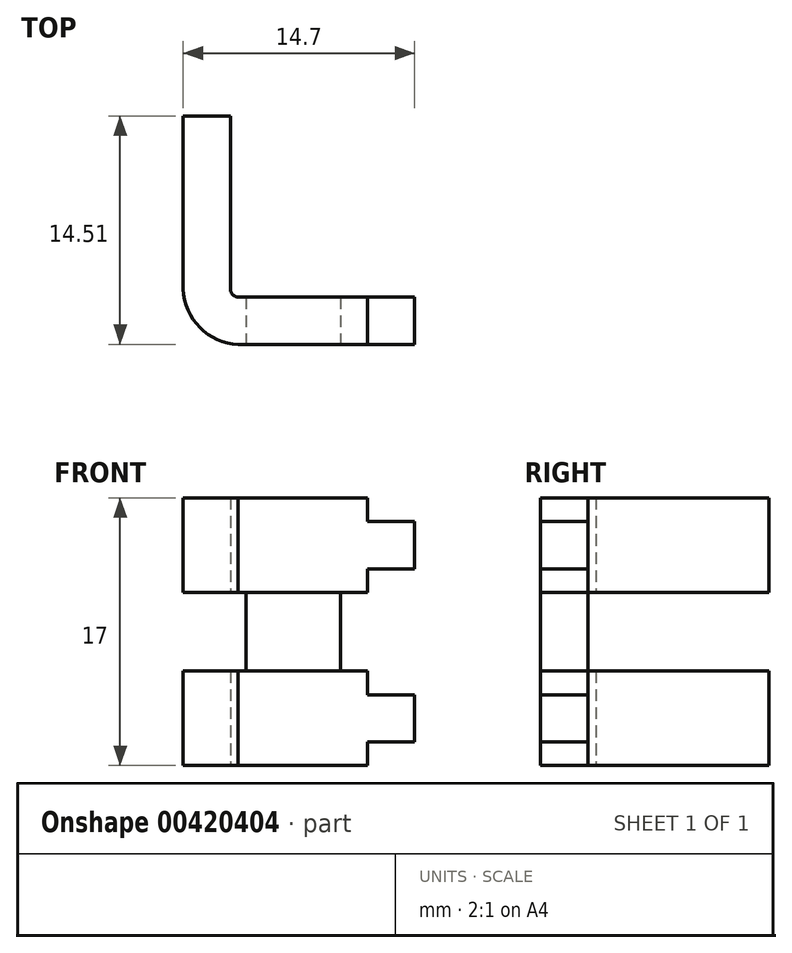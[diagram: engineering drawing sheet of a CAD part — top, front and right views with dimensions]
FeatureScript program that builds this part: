
annotation { "Feature Type Name" : "Feature", "Feature Type Description" : "" }
export const myFeature = defineFeature(function(context is Context, id is Id, definition is map)
    precondition{}
    {
        {
            var Q0;
            Q0=qCreatedBy(makeId("Top.planeOp"),FACE);
            var sketch = newSketch(context, id + "F0", { "sketchPlane" : qUnion([Q0])});
            skLineSegment(sketch, "E0", {"start": v(-1.5, 13) * mm, "end": v(1.5, 13) * mm});
            skLineSegment(sketch, "E1", {"start": v(13.2, 1.49) * mm, "end": v(13.2, -1.51) * mm});
            skArc(sketch, "E2", {"start": v(1.5, 2) * mm, "mid": v(1.65, 1.65) * mm, "end": v(2, 1.5) * mm});
            skLineSegment(sketch, "E3", {"start": v(2, 1.5) * mm, "end": v(13.2, 1.49) * mm});
            skLineSegment(sketch, "E4", {"start": v(1.5, 2) * mm, "end": v(1.5, 13) * mm});
            skArc(sketch, "E5", {"start": v(-1.5, 2) * mm, "mid": v(-0.44, -0.44) * mm, "end": v(2, -1.51) * mm});
            skLineSegment(sketch, "E6", {"start": v(-1.5, 2) * mm, "end": v(-1.5, 13) * mm});
            skLineSegment(sketch, "E7", {"start": v(2, -1.51) * mm, "end": v(13.2, -1.51) * mm});
            skSolve(sketch);
        }
        {
            var Q0;
            Q0 = qSketchRegion(id + "F0", true);
            extrude(context, id + "F1", {"entities" : qUnion([Q0]), "depth" : 6 * mm, "offsetDistance" : 25 * mm});
        }
        {
            var Q0;
            Q0=makeQuery(id+"F1.opExtrude","SWEPT_FACE",FACE,{"disambiguationData":[OSD([sQuery(id+"F0.wireOp",EDGE,"E7")])]});
            var sketch = newSketch(context, id + "F2", { "sketchPlane" : qUnion([Q0])});
            skLineSegment(sketch, "E8.bottom", {"start": v(13.2, 6) * mm, "end": v(10.2, 6) * mm});
            skLineSegment(sketch, "E8.top", {"start": v(13.2, 4.5) * mm, "end": v(10.2, 4.5) * mm});
            skLineSegment(sketch, "E8.left", {"start": v(13.2, 6) * mm, "end": v(13.2, 4.5) * mm});
            skLineSegment(sketch, "E8.right", {"start": v(10.2, 6) * mm, "end": v(10.2, 4.5) * mm});
            skLineSegment(sketch, "E9.bottom", {"start": v(13.2, 0) * mm, "end": v(10.2, 0) * mm});
            skLineSegment(sketch, "E9.top", {"start": v(13.2, 1.5) * mm, "end": v(10.2, 1.5) * mm});
            skLineSegment(sketch, "E9.left", {"start": v(13.2, 0) * mm, "end": v(13.2, 1.5) * mm});
            skLineSegment(sketch, "E9.right", {"start": v(10.2, 0) * mm, "end": v(10.2, 1.5) * mm});
            skSolve(sketch);
        }
        {
            var Q0;
            Q0 = qSketchRegion(id + "F2", true);
            extrude(context, id + "F3", {"entities" : qUnion([Q0]), "operationType" : NewBodyOperationType.REMOVE, "oppositeDirection" : true, "depth" : 3 * mm, "offsetDistance" : 25 * mm});
        }
        {
            var Q0;
            Q0=makeQuery(id+"F1.opExtrude","SWEPT_BODY",BODY,{"disambiguationData":[OSD([sQuery(id+"F0.wireOp",EDGE,"E0"),sQuery(id+"F0.wireOp",EDGE,"E1"),sQuery(id+"F0.wireOp",EDGE,"E2"),sQuery(id+"F0.wireOp",EDGE,"E3"),sQuery(id+"F0.wireOp",EDGE,"E4"),sQuery(id+"F0.wireOp",EDGE,"E5"),sQuery(id+"F0.wireOp",EDGE,"E6"),sQuery(id+"F0.wireOp",EDGE,"E7")])]});
            transform(context, id + "F4", {"entities" : qUnion([Q0]), "transformType" : TransformType.TRANSLATION_3D, "dx" : 0 * mm, "dy" : 0 * mm, "dz" : 11 * mm, "makeCopy" : true});
        }
        {
            var Q0;
            Q0=makeQuery(id+"F4.opPattern","COPY",FACE,{"derivedFrom":makeQuery(id+"F1.opExtrude","SWEPT_FACE",FACE,{"disambiguationData":[OSD([sQuery(id+"F0.wireOp",EDGE,"E7")])]}),"instanceName":"1"});
            var sketch = newSketch(context, id + "F5", { "sketchPlane" : qUnion([Q0])});
            skLineSegment(sketch, "E10.bottom", {"start": v(2.48, 11) * mm, "end": v(8.48, 11) * mm});
            skLineSegment(sketch, "E10.top", {"start": v(2.48, 6) * mm, "end": v(8.48, 6) * mm});
            skLineSegment(sketch, "E10.left", {"start": v(2.48, 11) * mm, "end": v(2.48, 6) * mm});
            skLineSegment(sketch, "E10.right", {"start": v(8.48, 11) * mm, "end": v(8.48, 6) * mm});
            skSolve(sketch);
        }
        {
            var Q0;
            Q0 = qSketchRegion(id + "F5", true);
            extrude(context, id + "F6", {"entities" : qUnion([Q0]), "oppositeDirection" : true, "depth" : 3 * mm, "offsetDistance" : 25 * mm});
        }
    });
